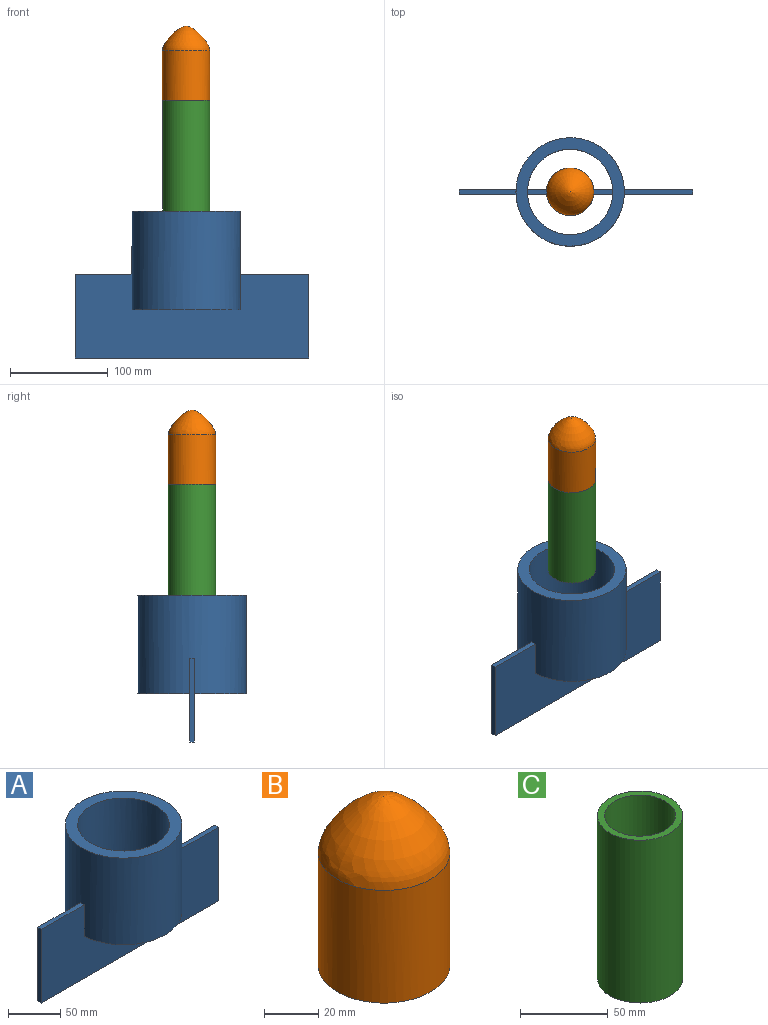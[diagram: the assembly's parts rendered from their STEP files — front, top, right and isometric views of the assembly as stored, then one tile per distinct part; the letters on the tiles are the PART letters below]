
ASSEMBLY  parts=3 mates=2
PART A: 13 faces, bbox 238.9x111x150.6 mm
  f0: plane 110.92x52.98mm, normal (0,0,-1), area 1776.8mm2, adj f1,f2,f8
  f1: cylinder r=43.74mm len=101.35mm, axis (0,0,1), area 27479.2mm2, adj f0,f3,f4,f5,f7,f8
  f2: cylinder r=55.52mm len=111.04mm, axis (0,0,1), area 34980.6mm2, adj f0,f3,f4,f6,f7,f8,f12
  f3: plane 110.92x52.98mm, normal (0,0,-1), area 1776.8mm2, adj f1,f2,f7
  f4: plane 111.04x111.04mm, normal (0,0,1), area 3673.4mm2, adj f1,f2
  f5: plane 87.48x5.08mm, normal (0,0,1), area 444.1mm2, adj f1,f7,f8
  f6: plane 57.98x5.08mm, normal (0,0,1), area 294.4mm2, adj f2,f7,f8,f9
  f7: plane 238.86x85.86mm, normal (0,-1,0), area 19643.2mm2, adj f1,f2,f3,f5,f6,f9,f10,f11
  f8: plane 238.86x85.86mm, normal (0,1,0), area 19643.2mm2, adj f0,f1,f2,f5,f6,f9,f10,f11
  f9: plane 85.86x5.08mm, normal (-1,0,0), area 436.2mm2, adj f6,f7,f8,f10
  f10: plane 238.86x5.08mm, normal (0,0,-1), area 1213.4mm2, adj f7,f8,f9,f11
  f11: plane 85.86x5.08mm, normal (1,0,0), area 436.2mm2, adj f7,f8,f10,f12
  f12: plane 69.95x5.08mm, normal (0,0,1), area 355.2mm2, adj f2,f7,f8,f11
PART B: 6 faces, bbox 58.7x58.7x86.4 mm
  f0: plane 40.41x40.41mm, normal (0,0,-1), area 124.9mm2, adj f1,f5
  f1: cylinder r=20.19mm len=50.8mm, axis (0,0,-1), area 6445.7mm2, adj f0,f3
  f2: cylinder r=24.26mm len=50.8mm, axis (0,0,-1), area 7744.5mm2, adj f3,f4
  f3: plane 48.53x48.53mm, normal (0,0,-1), area 568.3mm2, adj f1,f2
  f4: bspline ~48.53x48.53mm, area 3346.1mm2, adj f2
  f5: offset ~58.69x58.69mm, area 2026.2mm2, adj f0
PART C: 4 faces, bbox 48.5x48.5x113.3 mm
  f0: cylinder r=20.19mm len=113.28mm, axis (0,0,-1), area 14373.6mm2, adj f2,f3
  f1: cylinder r=24.26mm len=113.28mm, axis (0,0,-1), area 17270.4mm2, adj f2,f3
  f2: plane 48.53x48.53mm, normal (0,0,1), area 568.4mm2, adj f0,f1
  f3: plane 48.53x48.53mm, normal (0,0,-1), area 568.4mm2, adj f0,f1
PLACE A t=(-13.13,18.88,-16.95)mm
PLACE B t=(-13.13,18.88,96.33)mm
PLACE C t=(-13.13,18.88,-16.95)mm
MATE fastened B.f1 <-> C.f0  axis (0,0,-1) through (-13.13,18.88,96.33)mm
MATE fastened A.f1 <-> C.f0  axis (0,0,1) through (-13.13,18.88,-16.95)mm
